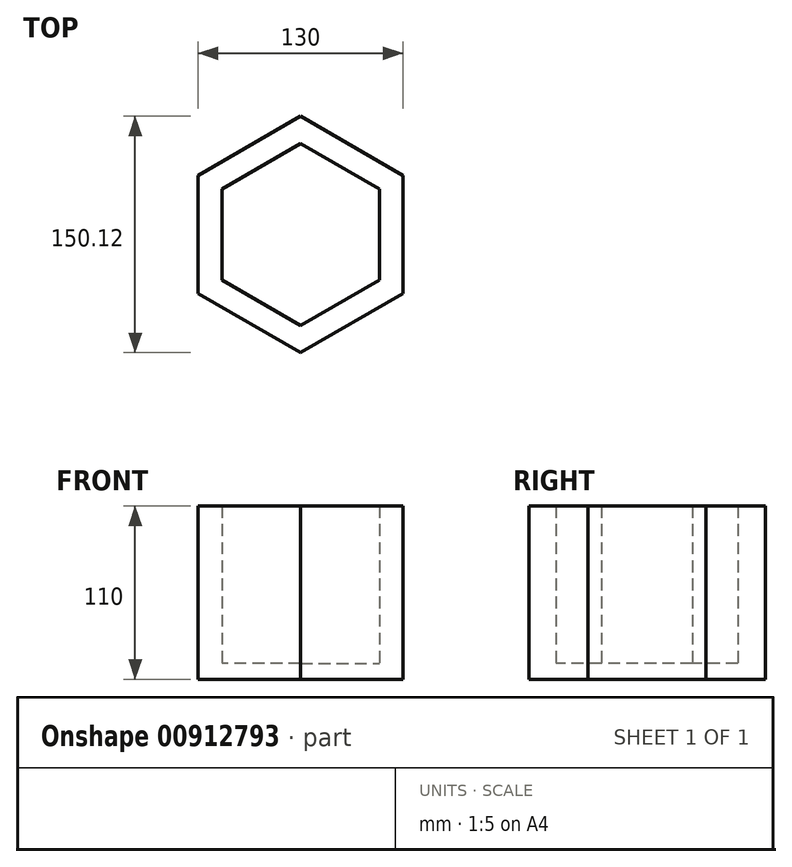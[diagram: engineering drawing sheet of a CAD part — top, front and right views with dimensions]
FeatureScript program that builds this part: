
annotation { "Feature Type Name" : "Feature", "Feature Type Description" : "" }
export const myFeature = defineFeature(function(context is Context, id is Id, definition is map)
    precondition{}
    {
        {
            var Q0;
            Q0=qCreatedBy(makeId("Top.planeOp"),FACE);
            var sketch = newSketch(context, id + "F0", { "sketchPlane" : qUnion([Q0])});
            skCircle(sketch, "E0.cCircle", {"center": v(0, 0) * mm, "radius": 50 * mm, "construction": true});
            skLineSegment(sketch, "E0.0", {"start": v(50, 28.87) * mm, "end": v(50, -28.87) * mm});
            skLineSegment(sketch, "E0.1", {"start": v(50, -28.87) * mm, "end": v(0, -57.74) * mm});
            skLineSegment(sketch, "E0.2", {"start": v(0, -57.74) * mm, "end": v(-50, -28.87) * mm});
            skLineSegment(sketch, "E0.3", {"start": v(-50, -28.87) * mm, "end": v(-50, 28.87) * mm});
            skLineSegment(sketch, "E0.4", {"start": v(-50, 28.87) * mm, "end": v(0, 57.74) * mm});
            skLineSegment(sketch, "E0.5", {"start": v(0, 57.74) * mm, "end": v(50, 28.87) * mm});
            skPoint(sketch, "E0.0.midPoint", {"position": v(50, 0) * mm});
            skLineSegment(sketch, "E1.0", {"start": v(-65, 37.53) * mm, "end": v(0, 75.06) * mm});
            skLineSegment(sketch, "E1.1", {"start": v(65, 37.53) * mm, "end": v(65, -37.53) * mm});
            skLineSegment(sketch, "E1.2", {"start": v(65, -37.53) * mm, "end": v(0, -75.06) * mm});
            skLineSegment(sketch, "E1.3", {"start": v(0, 75.06) * mm, "end": v(65, 37.53) * mm});
            skLineSegment(sketch, "E1.4", {"start": v(0, -75.06) * mm, "end": v(-65, -37.53) * mm});
            skLineSegment(sketch, "E1.5", {"start": v(-65, -37.53) * mm, "end": v(-65, 37.53) * mm});
            skSolve(sketch);
        }
        {
            var Q0;
            Q0=makeQuery(id+"F0.imprint","IMPRINT",FACE,{"disambiguationData":[TD([[makeQuery(id+"F0.imprint","IMPRINT",EDGE,{"derivedFrom":sQuery(id+"F0.wireOp",EDGE,"E0.0")}),1.0]])]});
            var Q1;
            Q1=makeQuery(id+"F0.imprint","IMPRINT",FACE,{"disambiguationData":[TD([[makeQuery(id+"F0.imprint","IMPRINT",EDGE,{"derivedFrom":sQuery(id+"F0.wireOp",EDGE,"E0.0")}),-1.0]])]});
            extrude(context, id + "F1", {"entities" : qUnion([Q0, Q1]), "oppositeDirection" : true, "depth" : 10 * mm, "offsetDistance" : 25 * mm});
        }
        {
            var Q0;
            Q0=makeQuery(id+"F0.imprint","IMPRINT",FACE,{"disambiguationData":[TD([[makeQuery(id+"F0.imprint","IMPRINT",EDGE,{"derivedFrom":sQuery(id+"F0.wireOp",EDGE,"E0.0")}),1.0]])]});
            extrude(context, id + "F2", {"entities" : qUnion([Q0]), "operationType" : NewBodyOperationType.ADD, "depth" : 100 * mm, "offsetDistance" : 25 * mm});
        }
    });
